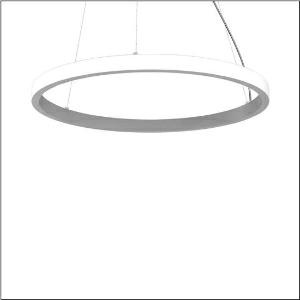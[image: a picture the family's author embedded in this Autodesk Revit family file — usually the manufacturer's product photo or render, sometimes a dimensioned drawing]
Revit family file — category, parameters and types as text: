
# Revit family: silica_r__21_ring-o_5pjbo4d1204a_97b4
name_source: partatom
category: Lighting Fixtures
units: mm (PartAtom-declared; Revit-internal decimal feet)

## family parameters
Cut with Voids When Loaded = No
Host = Face
Light Source = No
Part Type = Normal
Room Calculation Point = No
Round Connector Dimension = Use Diameter
Shared = No

## types (1)
- Silica® 21 Ring-O (1 x LED, 8820 lm, 343 W, 3000K)
    Apparent Load = 343 VA
    CIE Flux Codes = 2 16 49 50 100
    Color Rendering = 80
    Color Temperature = 3000K
    Default Elevation = 1800 mm
    Description = Silica® 21 Ring-O, suspended luminaire, of PMMA, frosted, light emission: outer ring side luminous distribution, primary light characteristic: symmetric, installation type: suspended mounting, LED, rated luminous flux: 8.820lm, luminous efficacy: 63lm/W, light colour: 830, colour temperature: 3000K, with terminal, 5-pole, mains connection: 230V, AC/DC, 0/50..60Hz, rated input power: 140W, housing, of extruded aluminium section, metallic grey (RAL 9006), diameter: 1.480mm, ceiling canopy, metallic grey (RAL 9006), protection rating (lamp compartment): IP40, insulation class (complete): insulation class I (protective earthing), certification: CE, impact resistance: IK02, permissible operating ambient temperature: 0..+35°C, packaging unit: 1 piece
    Height = 48 mm  [stored 0.15748 ft]
    Lamp = 1 x LED
    Lamp Light Flux = 8820 lm
    Lamp Power = 343 W
    Lamp count = 1
    Length = 1480 mm
    Luminous efficacy = 26 lm/W
    Manufacturer = Siteco
    ModVariant = No
    Model = 5PJBO4D1204A
    Mounting Place = Ceiling
    Mounting Type = Pendant
    Number of Poles = 1
    OnlyDefault = Yes
    Power Factor = 1
    Product Name = Silica® 21 Ring-O
    Product group = suspended luminaire
    ProductGroupID = 904
    Protection Class = Protection class I
    Protection Degree = IP 40
    RLX_Detail_Level = 1
    RLX_Emergency_Light_Flux = 0 lm
    RLX_Emergency_Type = 0
    RLX_Emergency_Type_DB = No
    RlxData = <blob elided: 18397 chars, md5=cf301076>
    Socket = socket
    Standby Power = 0 W
    System Light Flux = 8819 lm
    System Power = 343 W
    Type Comments = Product without accessories
    Type Image = l_1251764.jpg
    URL = http://relux.com
    VarID = ---
    Voltage = 0 V
    Weight = 0.00 kg
    Width = 0 mm  [stored 0 ft]

note: [stored X ft] marks values corroborated as IEEE doubles in the binary element streams (Revit-internal decimal feet)

## geometry (parser evidence)
native form markers: Blend x4, Sweep x11
no freeform markers — native parametric forms only
